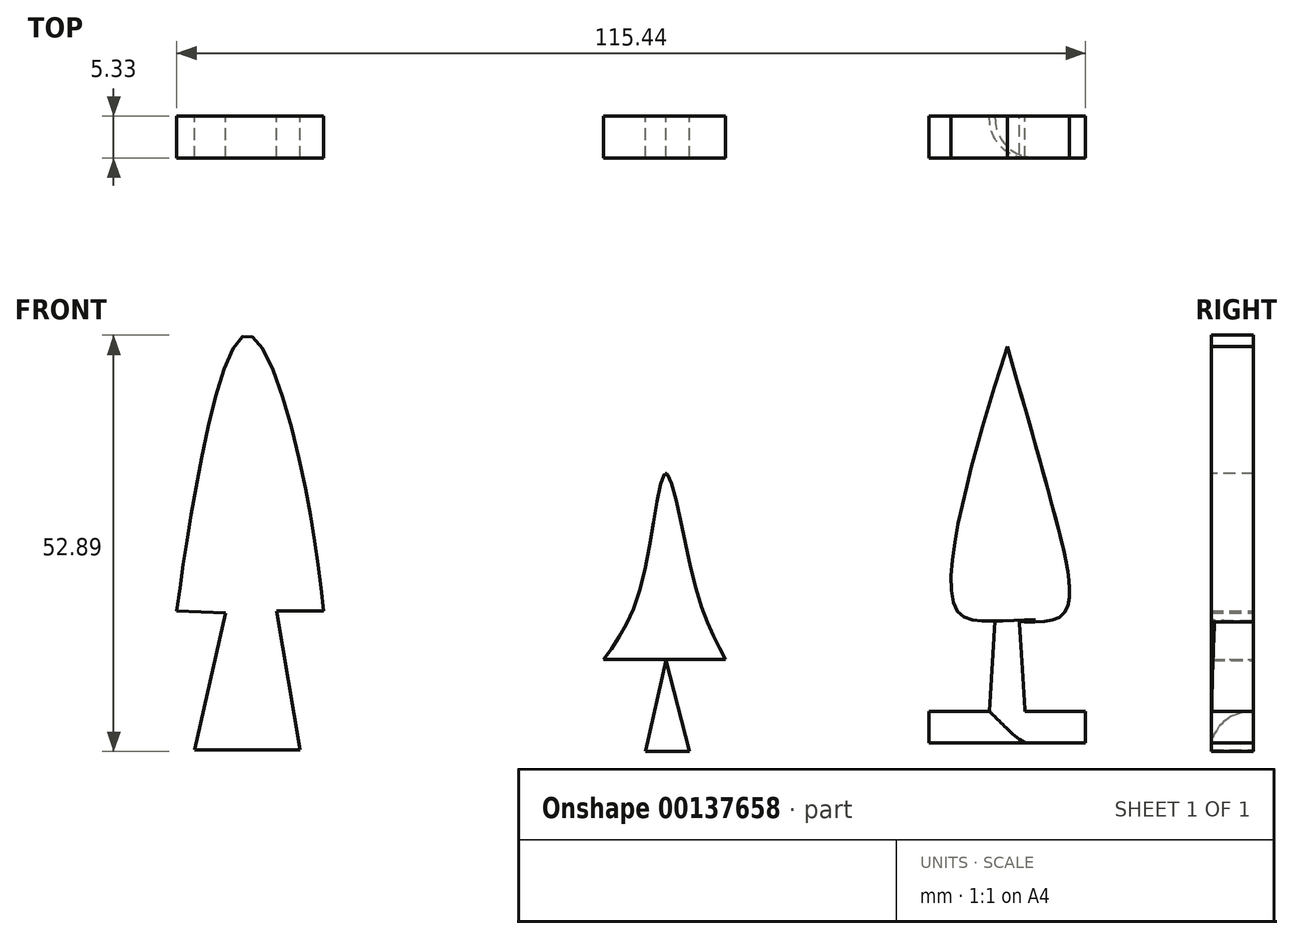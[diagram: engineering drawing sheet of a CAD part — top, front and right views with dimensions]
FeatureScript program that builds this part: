
annotation { "Feature Type Name" : "Feature", "Feature Type Description" : "" }
export const myFeature = defineFeature(function(context is Context, id is Id, definition is map)
    precondition{}
    {
        {
            var Q0;
            Q0=qCreatedBy(makeId("Front.planeOp"),FACE);
            var sketch = newSketch(context, id + "F0", { "sketchPlane" : qUnion([Q0])});
            skLineSegment(sketch, "E0", {"start": v(-55.9, 22.49) * mm, "end": v(-59.88, 5.1) * mm});
            skLineSegment(sketch, "E1", {"start": v(-59.88, 5.1) * mm, "end": v(-46.47, 5.1) * mm});
            skLineSegment(sketch, "E2", {"start": v(-46.47, 5.1) * mm, "end": v(-49.45, 22.74) * mm});
            skLineSegment(sketch, "E3", {"start": v(-49.45, 22.74) * mm, "end": v(-43.48, 22.74) * mm});
            skLineSegment(sketch, "E4", {"start": v(-55.9, 22.49) * mm, "end": v(-62.12, 22.74) * mm});
            skPoint(sketch, "E5.1.internal.snap0", {"position": v(-59.01, 22.61) * mm});
            skFitSpline(sketch, "E5", {"points": [v(-62.12, 22.74) * mm, v(-59.01, 41.87) * mm, v(-53.17, 57.77) * mm, v(-46.47, 41.62) * mm, v(-43.48, 22.74) * mm], "startDerivative": vector(9.2, 66.98) * mm, "endDerivative": vector(7.32, -66.35) * mm});
            skLineSegment(sketch, "E6", {"start": v(-2.56, 4.88) * mm, "end": v(3, 4.88) * mm});
            skLineSegment(sketch, "E7", {"start": v(3, 4.88) * mm, "end": v(0, 16.46) * mm});
            skLineSegment(sketch, "E8", {"start": v(0, 16.46) * mm, "end": v(-2.56, 4.88) * mm});
            skLineSegment(sketch, "E9", {"start": v(-4.01, 16.46) * mm, "end": v(3.47, 16.46) * mm});
            skSolve(sketch);
        }
        {
            var Q0;
            Q0=qCreatedBy(makeId("Front.planeOp"),FACE);
            var sketch = newSketch(context, id + "F1", { "sketchPlane" : qUnion([Q0])});
            skLineSegment(sketch, "E10", {"start": v(0, 16.55) * mm, "end": v(-7.93, 16.55) * mm});
            skLineSegment(sketch, "E11", {"start": v(-7.93, 16.55) * mm, "end": v(7.57, 16.55) * mm});
            skFitSpline(sketch, "E12", {"points": [v(-7.93, 16.55) * mm, v(-3.07, 26.17) * mm, v(0, 40.2) * mm, v(3.6, 26.4) * mm, v(7.57, 16.55) * mm], "startDerivative": vector(23.35, 31.47) * mm, "endDerivative": vector(17.76, -33.29) * mm});
            skLineSegment(sketch, "E13", {"start": v(33.43, 5.98) * mm, "end": v(53.32, 5.98) * mm});
            skLineSegment(sketch, "E14", {"start": v(53.32, 5.98) * mm, "end": v(53.32, 9.96) * mm});
            skLineSegment(sketch, "E15", {"start": v(53.32, 9.96) * mm, "end": v(33.43, 9.96) * mm});
            skLineSegment(sketch, "E16", {"start": v(33.43, 9.96) * mm, "end": v(33.43, 5.98) * mm});
            skPoint(sketch, "E17.endSnap0", {"position": v(43.37, 9.96) * mm});
            skLineSegment(sketch, "E18", {"start": v(43.37, 46.03) * mm, "end": v(41.12, 9.96) * mm});
            skLineSegment(sketch, "E19", {"start": v(43.37, 46.03) * mm, "end": v(45.63, 9.96) * mm});
            skFitSpline(sketch, "E20", {"points": [v(43.37, 56.3) * mm, v(37.18, 34) * mm, v(37.18, 22.5) * mm, v(41.84, 21.45) * mm], "startDerivative": vector(-15.43, -49.3) * mm, "endDerivative": vector(26.17, 0.82) * mm});
            skFitSpline(sketch, "E21", {"points": [v(43.37, 56.3) * mm, v(49.65, 34) * mm, v(50.6, 22.5) * mm, v(44.91, 21.4) * mm], "startDerivative": vector(14.68, -50.49) * mm, "endDerivative": vector(-30.83, 1.43) * mm});
            skSolve(sketch);
        }
        {
            var Q0;
            {var subQ3=sQuery(id+"F1.wireOp",EDGE,"E20");Q0=makeQuery(id+"F1.imprint","IMPRINT",FACE,{"disambiguationData":[TD([[makeQuery(id+"F1.imprint","IMPRINT",EDGE,{"derivedFrom":subQ3}),1.0]])]});}
            var Q1;
            Q1=makeQuery(id+"F1.imprint","IMPRINT",FACE,{"disambiguationData":[TD([[makeQuery(id+"F1.imprint","IMPRINT",EDGE,{"derivedFrom":sQuery(id+"F1.wireOp",EDGE,"E13")}),1.0]])]});
            var Q2;
            {var subQ0=sQuery(id+"F1.wireOp",EDGE,"E18");var subQ1=sQuery(id+"F1.wireOp",EDGE,"E15");var subQ2=makeQuery(id+"F1.imprint","INTERSECT",VERTEX,{"derivedFrom":[subQ1,subQ0]});Q2=makeQuery(id+"F1.imprint","IMPRINT",FACE,{"disambiguationData":[TD([[makeQuery(id+"F1.imprint","IMPRINT",EDGE,{"disambiguationData":[TD([[subQ2,1.0]])],"derivedFrom":subQ1}),-1.0]])]});}
            var Q3;
            {var subQ0=sQuery(id+"F1.wireOp",EDGE,"E12");Q3=makeQuery(id+"F1.imprint","IMPRINT",FACE,{"disambiguationData":[TD([[makeQuery(id+"F1.imprint","IMPRINT",EDGE,{"derivedFrom":subQ0}),-1.0]])]});}
            var Q4;
            Q4=makeQuery(id+"F0.imprint","IMPRINT",FACE,{"disambiguationData":[TD([[makeQuery(id+"F0.imprint","IMPRINT",EDGE,{"derivedFrom":sQuery(id+"F0.wireOp",EDGE,"E6")}),1.0]])]});
            var Q5;
            Q5=makeQuery(id+"F0.imprint","IMPRINT",FACE,{"disambiguationData":[TD([[makeQuery(id+"F0.imprint","IMPRINT",EDGE,{"derivedFrom":sQuery(id+"F0.wireOp",EDGE,"E0")}),1.0]])]});
            extrude(context, id + "F2", {"entities" : qUnion([Q0, Q1, Q2, Q3, Q4, Q5]), "depth" : 5.33 * mm});
        }
        {
            var Q0;
            {var subQ0=sQuery(id+"F1.wireOp",EDGE,"E15");Q0=makeQuery(id+"F2.opExtrude","CAP_EDGE",EDGE,{"disambiguationData":[OSD([subQ0]),TDD([makeQuery(id+"F1.imprint","IMPRINT",EDGE,{"disambiguationData":[TD([[makeQuery(id+"F1.imprint","INTERSECT",VERTEX,{"derivedFrom":[subQ0,sQuery(id+"F1.wireOp",EDGE,"E16")]}),1.0]])],"derivedFrom":subQ0})])],"isStart":false});}
            var Q1;
            Q1=makeQuery(id+"F2.opExtrude","CAP_EDGE",EDGE,{"disambiguationData":[OSD([sQuery(id+"F1.wireOp",EDGE,"E18")])],"isStart":false});
            fillet(context, id + "F3", {"entities" : qUnion([Q0, Q1]), "radius" : 5.08 * mm, "tangentPropagation" : true, "allowEdgeOverflow" : false});
        }
    });
